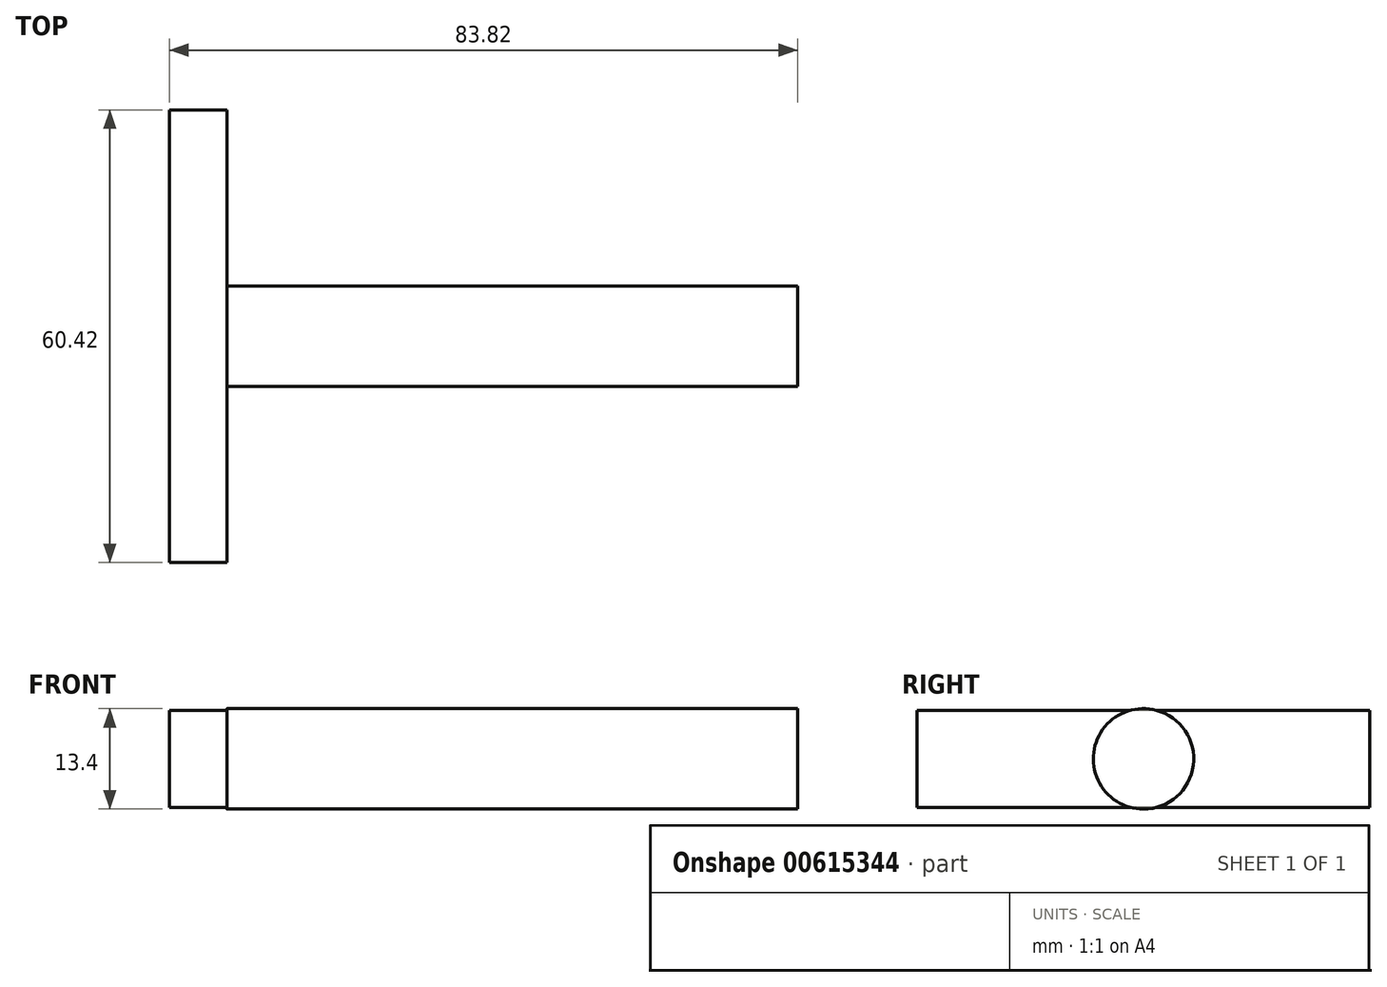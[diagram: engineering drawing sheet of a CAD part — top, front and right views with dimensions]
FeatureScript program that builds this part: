
annotation { "Feature Type Name" : "Feature", "Feature Type Description" : "" }
export const myFeature = defineFeature(function(context is Context, id is Id, definition is map)
    precondition{}
    {
        {
            var Q0;
            Q0=qCreatedBy(makeId("Right.planeOp"),FACE);
            var sketch = newSketch(context, id + "F0", { "sketchPlane" : qUnion([Q0])});
            skCircle(sketch, "E0", {"center": v(0, 0) * mm, "radius": 6.7 * mm});
            skSolve(sketch);
        }
        {
            var Q0;
            Q0 = qSketchRegion(id + "F0", true);
            extrude(context, id + "F1", {"entities" : qUnion([Q0]), "depth" : 76.2 * mm, "offsetDistance" : 25.4 * mm});
        }
        {
            var Q0;
            Q0=makeQuery(id+"F1.opExtrude","CAP_FACE",FACE,{"disambiguationData":[OSD([sQuery(id+"F0.wireOp",EDGE,"E0")])],"isStart":true});
            var sketch = newSketch(context, id + "F2", { "sketchPlane" : qUnion([Q0])});
            skLineSegment(sketch, "E1.bottom", {"start": v(-30.21, -6.48) * mm, "end": v(30.21, -6.48) * mm});
            skLineSegment(sketch, "E1.top", {"start": v(-30.21, 6.48) * mm, "end": v(30.21, 6.48) * mm});
            skLineSegment(sketch, "E1.left", {"start": v(-30.21, -6.48) * mm, "end": v(-30.21, 6.48) * mm});
            skLineSegment(sketch, "E1.right", {"start": v(30.21, -6.48) * mm, "end": v(30.21, 6.48) * mm});
            skPoint(sketch, "E1.middle", {"position": v(0, 0) * mm});
            skSolve(sketch);
        }
        {
            var Q0;
            Q0 = qSketchRegion(id + "F2", true);
            extrude(context, id + "F3", {"entities" : qUnion([Q0]), "operationType" : NewBodyOperationType.ADD, "depth" : 7.62 * mm, "offsetDistance" : 25.4 * mm});
        }
    });
